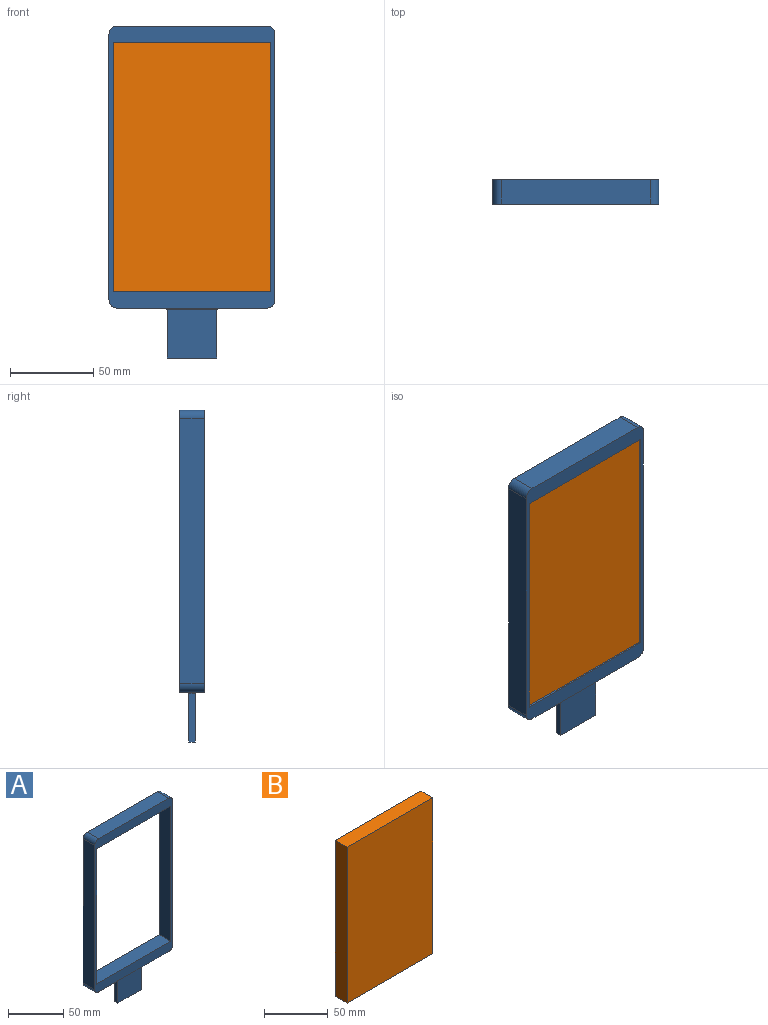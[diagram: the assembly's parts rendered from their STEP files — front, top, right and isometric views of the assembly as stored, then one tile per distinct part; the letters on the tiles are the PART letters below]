
ASSEMBLY  parts=2 mates=1
PART A: 23 faces, bbox 100x15x200 mm
  f0: plane 170x100mm, normal (0,-1,0), area 2728.5mm2, adj f2,f3,f4,f5,f6,f7,f8,f9
  f1: plane 170x100mm, normal (0,1,0), area 2728.5mm2, adj f2,f3,f4,f5,f6,f7,f8,f9
  f2: plane 90x15mm, normal (0,0,1), area 1350mm2, adj f0,f1,f6,f9
  f3: plane 160x15mm, normal (-1,0,0), area 2400mm2, adj f0,f1,f6,f7
  f4: plane 90x15mm, normal (0,0,-1), area 1158mm2, adj f0,f1,f7,f8,f19,f20,f21,f22
  f5: plane 160x15mm, normal (1,0,0), area 2400mm2, adj f0,f1,f8,f9
  f6: cylinder r=5mm len=15mm, axis (0,-1,0), area 117.8mm2, adj f0,f1,f2,f3
  f7: cylinder r=5mm len=15mm, axis (0,1,0), area 117.8mm2, adj f0,f1,f3,f4
  f8: cylinder r=5mm len=15mm, axis (0,-1,0), area 117.8mm2, adj f0,f1,f4,f5
  f9: cylinder r=5mm len=15mm, axis (0,1,0), area 117.8mm2, adj f0,f1,f2,f5
  f10: plane 95x15mm, normal (0,0,1), area 1425mm2, adj f0,f1,f11,f13
  f11: plane 150x15mm, normal (-1,0,0), area 2250mm2, adj f0,f1,f10,f12
  f12: plane 95x15mm, normal (0,0,-1), area 1425mm2, adj f0,f1,f11,f13
  f13: plane 150x15mm, normal (1,0,0), area 2250mm2, adj f0,f1,f10,f12
  f14: plane 30x29mm, normal (0,1,0), area 870mm2, adj f15,f17,f18,f19
  f15: plane 29x4mm, normal (1,0,0), area 116mm2, adj f14,f16,f18,f20
  f16: plane 30x29mm, normal (0,-1,0), area 870mm2, adj f15,f17,f18,f22
  f17: plane 29x4mm, normal (-1,0,0), area 116mm2, adj f14,f16,f18,f21
  f18: plane 30x4mm, normal (0,0,-1), area 120mm2, adj f14,f15,f16,f17
  f19: cylinder r=1mm len=32mm, axis (-1,0,0), area 48.3mm2, adj f4,f14,f20,f21
  f20: cylinder r=1mm len=6mm, axis (0,1,0), area 7.4mm2, adj f4,f15,f19,f22
  f21: cylinder r=1mm len=6mm, axis (0,-1,0), area 7.4mm2, adj f4,f17,f19,f22
  f22: cylinder r=1mm len=32mm, axis (1,0,0), area 48.3mm2, adj f4,f16,f20,f21
PART B: 6 faces, bbox 95x13x150 mm
  f0: plane 95x13mm, normal (0,0,1), area 1235mm2, adj f1,f3,f4,f5
  f1: plane 150x13mm, normal (-1,0,0), area 1950mm2, adj f0,f2,f4,f5
  f2: plane 95x13mm, normal (0,0,-1), area 1235mm2, adj f1,f3,f4,f5
  f3: plane 150x13mm, normal (1,0,0), area 1950mm2, adj f0,f2,f4,f5
  f4: plane 150x95mm, normal (0,-1,0), area 14250mm2, adj f0,f1,f2,f3
  f5: plane 150x95mm, normal (0,1,0), area 14250mm2, adj f0,f1,f2,f3
PLACE A t=(-311.83,-185.03,-13.89)mm
PLACE B t=(-311.39,-186.03,-11.55)mm
MATE fastened B.f0 <-> A.f12  axis (0,0,1) through (-323.04,-192.53,70.8)mm
